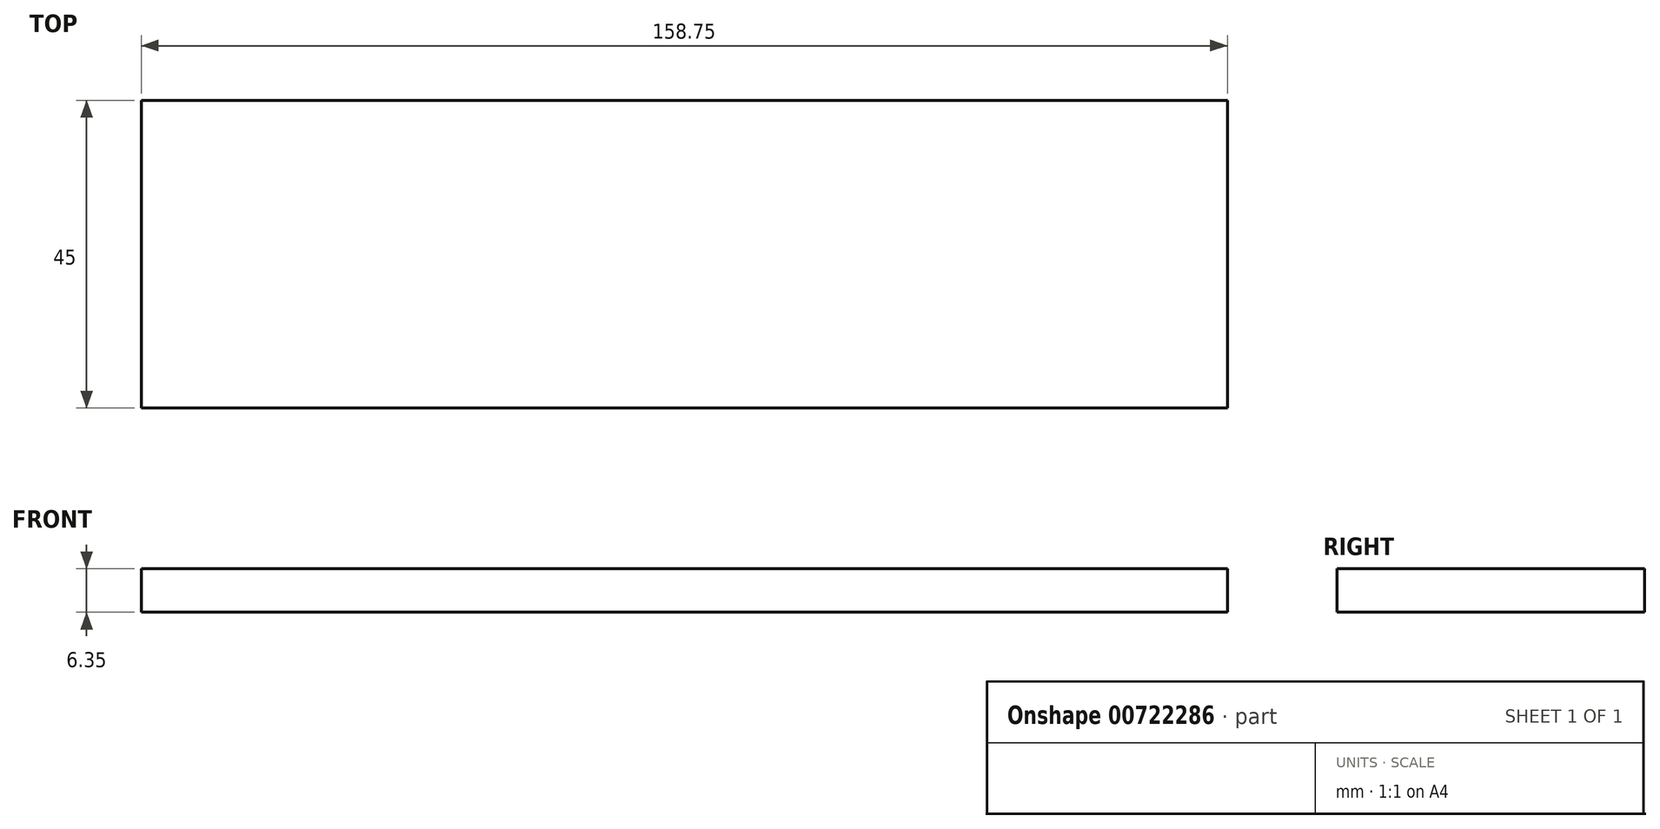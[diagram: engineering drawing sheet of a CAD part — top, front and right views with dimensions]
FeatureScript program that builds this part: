
annotation { "Feature Type Name" : "Feature", "Feature Type Description" : "" }
export const myFeature = defineFeature(function(context is Context, id is Id, definition is map)
    precondition{}
    {
        {
            var Q0;
            Q0=qCreatedBy(makeId("Top.planeOp"),FACE);
            var sketch = newSketch(context, id + "F0", { "sketchPlane" : qUnion([Q0])});
            skLineSegment(sketch, "E0.bottom", {"start": v(0, 0) * mm, "end": v(158.75, 0) * mm});
            skLineSegment(sketch, "E0.top", {"start": v(0, -45) * mm, "end": v(158.75, -45) * mm});
            skLineSegment(sketch, "E0.left", {"start": v(0, 0) * mm, "end": v(0, -45) * mm});
            skLineSegment(sketch, "E0.right", {"start": v(158.75, 0) * mm, "end": v(158.75, -45) * mm});
            skSolve(sketch);
        }
        {
            var Q0;
            Q0=makeQuery(id+"F0.imprint","IMPRINT",FACE,{"disambiguationData":[TD([[makeQuery(id+"F0.imprint","IMPRINT",EDGE,{"derivedFrom":sQuery(id+"F0.wireOp",EDGE,"E0.bottom")}),-1.0]])]});
            extrude(context, id + "F1", {"entities" : qUnion([Q0]), "depth" : 6.35 * mm, "offsetDistance" : 25.4 * mm});
        }
    });
